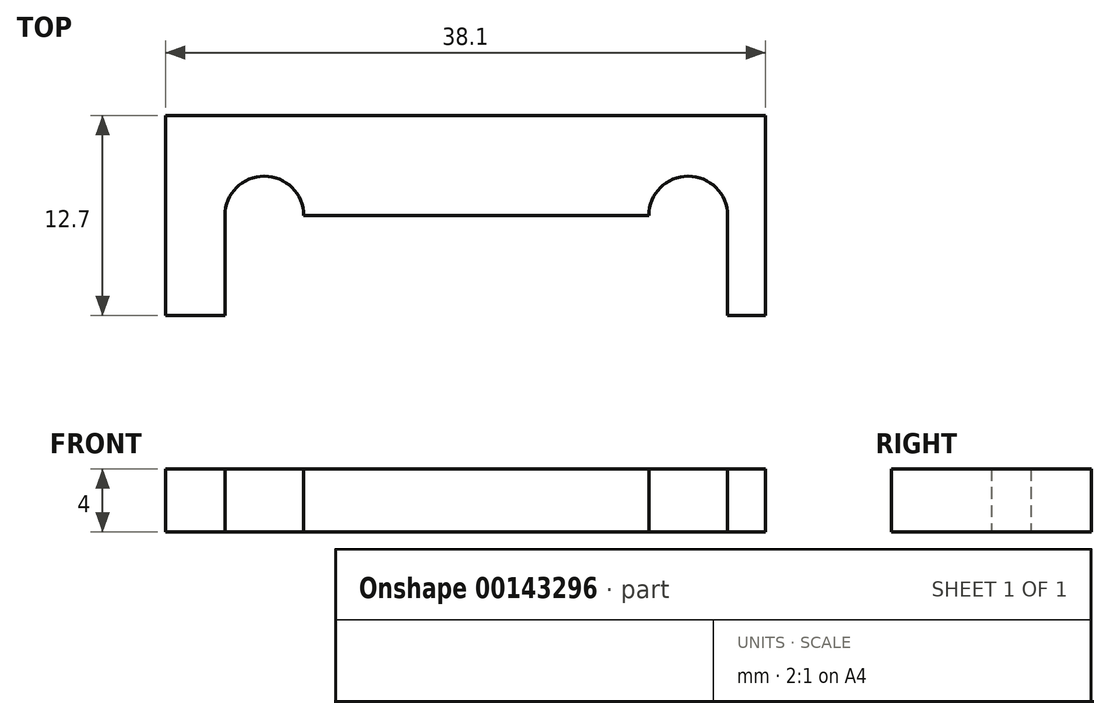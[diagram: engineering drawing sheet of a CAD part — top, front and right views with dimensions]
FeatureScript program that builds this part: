
annotation { "Feature Type Name" : "Feature", "Feature Type Description" : "" }
export const myFeature = defineFeature(function(context is Context, id is Id, definition is map)
    precondition{}
    {
        {
            var Q0;
            Q0=qCreatedBy(makeId("Top.planeOp"),FACE);
            var sketch = newSketch(context, id + "F0", { "sketchPlane" : qUnion([Q0])});
            skLineSegment(sketch, "E0", {"start": v(-12.78, 0) * mm, "end": v(14.14, 0) * mm});
            skLineSegment(sketch, "E1", {"start": v(14.14, 0) * mm, "end": v(-12.78, 0) * mm});
            skCircle(sketch, "E2", {"center": v(-12.78, 0) * mm, "radius": 2.5 * mm});
            skCircle(sketch, "E3", {"center": v(14.14, 0) * mm, "radius": 2.5 * mm});
            skLineSegment(sketch, "E4.bottom", {"start": v(19.05, -6.35) * mm, "end": v(-19.05, -6.35) * mm});
            skLineSegment(sketch, "E4.top", {"start": v(19.05, 6.35) * mm, "end": v(-19.05, 6.35) * mm});
            skLineSegment(sketch, "E4.left", {"start": v(19.05, -6.35) * mm, "end": v(19.05, 6.35) * mm});
            skLineSegment(sketch, "E4.right", {"start": v(-19.05, -6.35) * mm, "end": v(-19.05, 6.35) * mm});
            skPoint(sketch, "E4.middle", {"position": v(0, 0) * mm});
            skLineSegment(sketch, "E5", {"start": v(-15.28, 0) * mm, "end": v(-15.28, -6.35) * mm});
            skLineSegment(sketch, "E6", {"start": v(-15.28, -6.35) * mm, "end": v(-15.28, 0) * mm});
            skLineSegment(sketch, "E7", {"start": v(-10.28, 0) * mm, "end": v(-10.28, -6.35) * mm});
            skLineSegment(sketch, "E8", {"start": v(-10.28, -6.35) * mm, "end": v(-10.28, 0) * mm});
            skLineSegment(sketch, "E9", {"start": v(11.64, 0) * mm, "end": v(11.64, -6.35) * mm});
            skLineSegment(sketch, "E10", {"start": v(11.64, -6.35) * mm, "end": v(11.64, 0) * mm});
            skLineSegment(sketch, "E11", {"start": v(16.64, 0) * mm, "end": v(16.64, -6.35) * mm});
            skLineSegment(sketch, "E12", {"start": v(16.64, -6.35) * mm, "end": v(16.64, 0) * mm});
            skSolve(sketch);
        }
        {
            var Q0;
            Q0=makeQuery(id+"F0.imprint","IMPRINT",FACE,{"disambiguationData":[TD([[makeQuery(id+"F0.imprint","IMPRINT",EDGE,{"derivedFrom":sQuery(id+"F0.wireOp",EDGE,"E4.top")}),1.0]])]});
            var Q1;
            {var subQ0=sQuery(id+"F0.wireOp",EDGE,"E8");Q1=makeQuery(id+"F0.imprint","IMPRINT",FACE,{"disambiguationData":[TD([[makeQuery(id+"F0.imprint","IMPRINT",EDGE,{"derivedFrom":subQ0}),-1.0]])]});}
            extrude(context, id + "F1", {"entities" : qUnion([Q0, Q1]), "depth" : 4 * mm});
        }
    });
